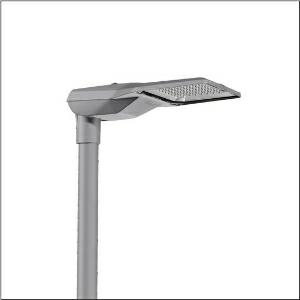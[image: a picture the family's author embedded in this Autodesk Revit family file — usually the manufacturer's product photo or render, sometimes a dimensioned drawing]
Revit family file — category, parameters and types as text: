
# Revit family: streetlight_sl_21_iq_midi___st1_0ab_5xe3m31v08mb_24a1
name_source: partatom
category: Lighting Fixtures
units: mm (PartAtom-declared; Revit-internal decimal feet)

## family parameters
Cut with Voids When Loaded = No
Host = Face
Light Source = No
Part Type = Normal
Room Calculation Point = No
Round Connector Dimension = Use Diameter
Shared = No

## types (1)
- --- (1 x LED, 16140 lm, 129.3 W, 3000K)
    Apparent Load = 129 VA
    CIE Flux Codes = 38 73 97 100 100
    Color Rendering = 70
    Color Temperature = 3000K
    Default Elevation = 1800 mm
    Description = Streetlight SL 21 iQ midi, mast luminaire, primary light control with lens, of PMMA, primary optical cover: cover, of toughened safety glass, transparent, light distribution: ST1.0aB, light emission: direct distribution, primary light characteristic: asymmetric, installation type: post-top, side-entry, LED, High Power LED, rated luminous flux: 16.140lm, luminous efficacy: 125lm/W, light colour: 730, colour temperature: 3000K, control gear: iQ-Street Remote, D4i with power reduction, control: pre-setting: logarithmic dimming characteristic, Street-Remote, Auto-Match, Temp-Guard, Lumen-Switch, Night-Set, Smart-Wire, Light-Fading, Desk-Remote (wireless, voltage-free reading and setting of iQ features in the workshop via application-optimized NFC function/RFID function), optimised constant luminous flux control (CLO 2.0), mains connection: 230..240V, AC, 50/60Hz, start of lifetime: 129W, end of service life: 142W, reduction: 56W, luminaire housing, of diecast aluminium, powder-coated, SITECO metallic grey (DB 702S), corrosivity category C5 high according to DIN EN ISO 12944, please order mast flange separately, inclination adjustable: 0°, 5°, 10°, 15°, sealing non-destructively replaceable, multi-level sealing system, length: 644mm, width: 335mm, height: 110mm, mast flange for spigot size: 42mm (side-entry): 5XC10008XM4, 60/48mm (side-entry/post-top): 5XC10108XM2, 76/60mm (side-entry/post-top): 5XC10108XM1, mounting height: 4..8m, Smart Interface above, protection rating (complete): IP66, insulation class (complete): insulation class II (safety insulation), certification: CE, ENEC, ENEC+, VDE, impact resistance: IK10, permissible operating ambient temperature for outdoor applications: -40..+50°C, standard-compliant lighting for roads and squares, packaging unit: 1 piece

Light Distribution: ST1.0aB
    Height = 111 mm
    Lamp = 1 x LED
    Lamp Light Flux = 16140 lm
    Lamp Power = 129.3 W
    Lamp count = 1
    Length = 644 mm
    Luminous efficacy = 125 lm/W
    Manufacturer = Siteco
    ModVariant = No
    Model = 5XE3M31V08MB
    Number of Poles = 1
    OnlyDefault = Yes
    Power Factor = 1
    Product Name = Streetlight SL 21 iQ midi | ST1.0aB
    Product group = mast luminaire | pylon top
    ProductGroupID = 6100
    Protection Class = Protection class II
    Protection Degree = IP 66
    RLX_Detail_Level = 1
    RLX_Emergency_Light_Flux = 0 lm
    RLX_Emergency_Type = 0
    RLX_Emergency_Type_DB = No
    RlxData = <blob elided: 91173 chars, md5=889656b7>
    Socket = socket
    Standby Power = 0 W
    System Light Flux = 16141 lm
    System Power = 129 W
    Type Comments = factory setting: luminous flux: 100 % | dim-lin: 254 | 672 mA
    Type Image = l_1004302.jpg
    URL = http://relux.com
    VarID = @adj_112315
    Voltage = 0 V
    Weight = 0.00 kg
    Width = 336 mm

## geometry (parser evidence)
native form markers: Blend x4, Sweep x11
no freeform markers — native parametric forms only
